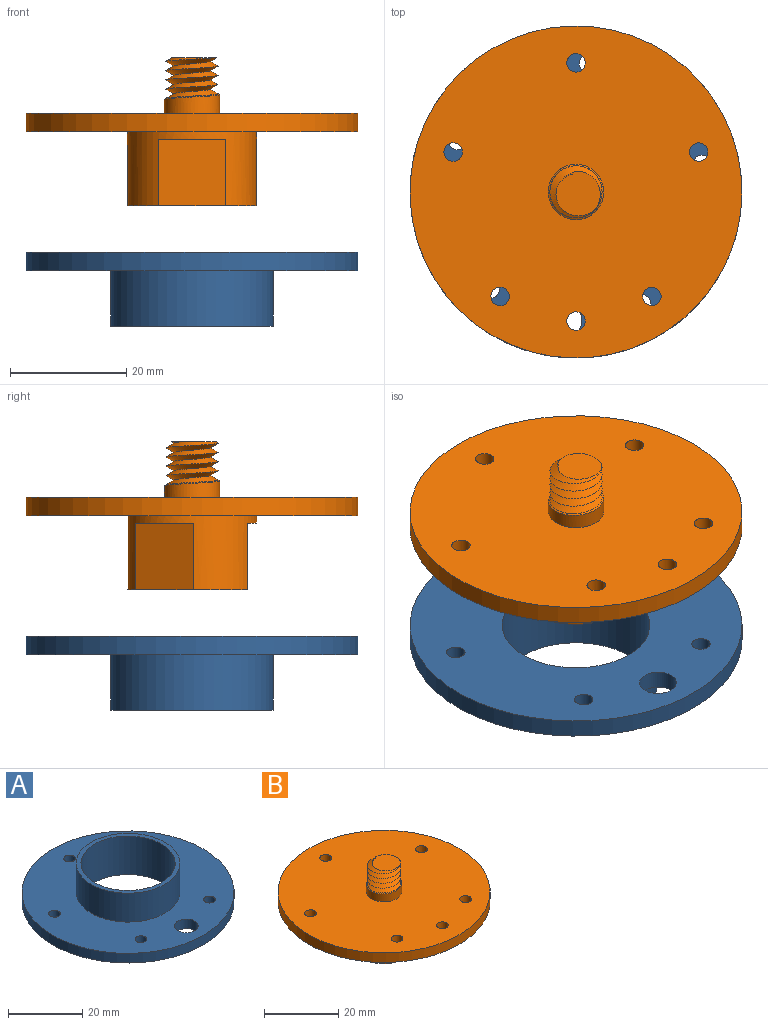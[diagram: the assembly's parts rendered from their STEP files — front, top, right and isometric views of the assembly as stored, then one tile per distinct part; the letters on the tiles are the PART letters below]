
ASSEMBLY  parts=2 mates=1
PART A: 12 faces, bbox 57.2x57.2x12.7 mm
  f0: cylinder r=1.59mm len=3.18mm, axis (0,0,-1), area 31.7mm2, adj f7,f8
  f1: cylinder r=1.59mm len=3.18mm, axis (0,0,-1), area 31.7mm2, adj f7,f8
  f2: cylinder r=1.59mm len=3.18mm, axis (0,0,-1), area 31.7mm2, adj f7,f8
  f3: cylinder r=1.59mm len=3.18mm, axis (0,0,-1), area 31.7mm2, adj f7,f8
  f4: cylinder r=1.59mm len=3.18mm, axis (0,0,-1), area 31.7mm2, adj f7,f8
  f5: cylinder r=3.17mm len=6.35mm, axis (0,0,-1), area 63.3mm2, adj f7,f8
  f6: cylinder r=28.57mm len=57.15mm, axis (0,0,-1), area 570mm2, adj f7,f8
  f7: plane 57.15x57.15mm, normal (0,0,1), area 1880.8mm2, adj f0,f1,f2,f3,f4,f5,f6,f9
  f8: plane 57.15x57.15mm, normal (0,0,-1), area 1987.2mm2, adj f0,f1,f2,f3,f4,f5,f6,f11
  f9: cylinder r=13.97mm len=27.94mm, axis (0,0,-1), area 836.1mm2, adj f7,f10
  f10: plane 27.94x27.94mm, normal (0,0,1), area 106.4mm2, adj f9,f11
  f11: cylinder r=12.7mm len=25.4mm, axis (0,0,1), area 1013.4mm2, adj f8,f10
PART B: 23 faces, bbox 58.3x58.3x27.5 mm
  f0: plane 22.22x20.64mm, normal (0,0,-1), area 351mm2, adj f11,f13,f15,f17
  f1: cylinder r=28.57mm len=57.15mm, axis (0,0,-1), area 570mm2, adj f2,f3
  f2: plane 57.15x57.15mm, normal (0,0,1), area 2446.4mm2, adj f1,f4,f5,f6,f7,f8,f9,f10
  f3: plane 57.15x57.15mm, normal (0,0,-1), area 2129.8mm2, adj f1,f5,f6,f7,f8,f9,f10,f11
  f4: cylinder r=4.76mm len=9.53mm, axis (0,0,-1), area 71.7mm2, adj f2,f18,f20
  f5: cylinder r=1.59mm len=3.18mm, axis (0,0,-1), area 31.7mm2, adj f2,f3
  f6: cylinder r=1.59mm len=3.18mm, axis (0,0,-1), area 31.7mm2, adj f2,f3
  f7: cylinder r=1.59mm len=3.18mm, axis (0,0,-1), area 31.7mm2, adj f2,f3
  f8: cylinder r=1.59mm len=3.18mm, axis (0,0,-1), area 31.7mm2, adj f2,f3
  f9: cylinder r=1.59mm len=3.18mm, axis (0,0,-1), area 31.7mm2, adj f2,f3
  f10: cylinder r=1.59mm len=3.18mm, axis (0,0,-1), area 31.7mm2, adj f2,f3
  f11: cylinder r=11.11mm len=22.23mm, axis (0,0,1), area 474.4mm2, adj f0,f3,f12,f13,f14,f15,f16,f17
  f12: plane 9.91x5.73mm, normal (0,0,-1), area 12.3mm2, adj f11,f13
  f13: plane 11.43x9.91mm, normal (-0.87,0.5,0), area 130.8mm2, adj f0,f11,f12
  f14: plane 9.91x5.73mm, normal (0,0,-1), area 12.3mm2, adj f11,f15
  f15: plane 11.43x9.91mm, normal (0.87,0.5,0), area 130.8mm2, adj f0,f11,f14
  f16: plane 11.45x1.59mm, normal (0,0,-1), area 12.3mm2, adj f11,f17
  f17: plane 11.45x11.43mm, normal (0,-1,0), area 130.8mm2, adj f0,f11,f16
  f18: plane 1.75x1.66mm, normal (0,1,0), area 1.5mm2, adj f4,f19,f20,f21
  f19: bspline ~10.35x8.96mm, area 176.4mm2, adj f18,f20,f21,f22
  f20: bspline ~11x9.53mm, area 9.4mm2, adj f4,f18,f19
  f21: bspline ~10.35x8.96mm, area 156.5mm2, adj f18,f19,f22
  f22: plane 8.79x8.78mm, normal (0,0,1), area 45.7mm2, adj f19,f21
PLACE A rot(axis=(-0.05,-1,0),180deg) t=(0,0,-20.75)mm
PLACE B at identity fixed
MATE cylindrical A.f11 <-> B.f11  axis (0,0,-1) through (0,0,-27.1)mm
